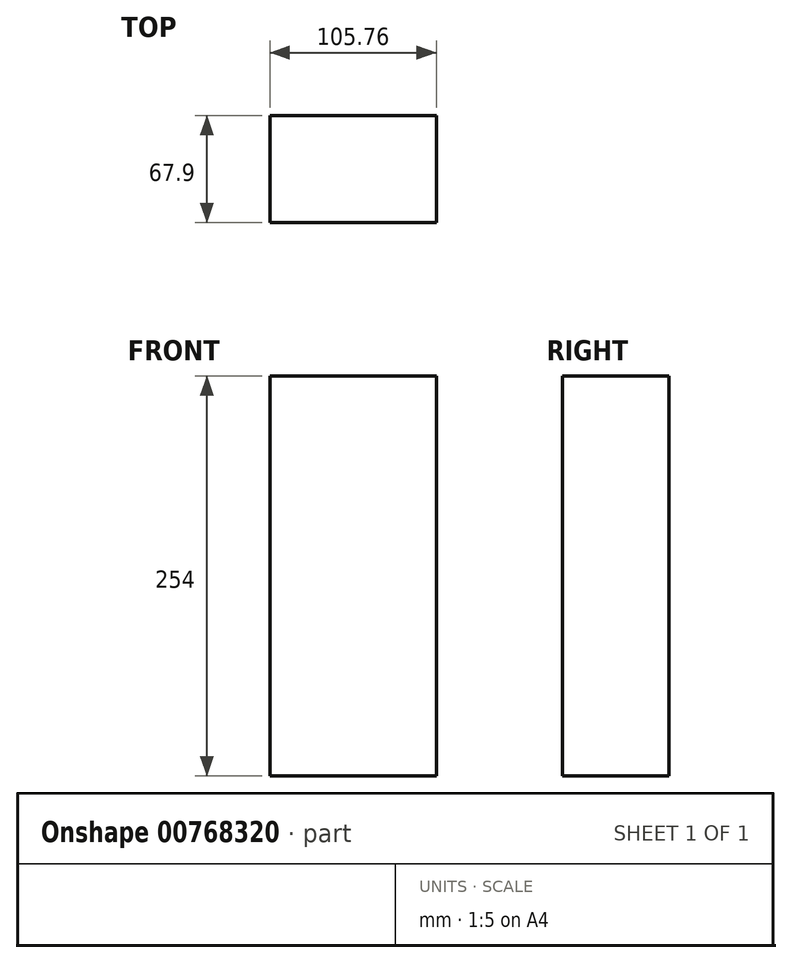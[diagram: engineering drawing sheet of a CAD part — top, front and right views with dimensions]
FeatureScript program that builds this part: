
annotation { "Feature Type Name" : "Feature", "Feature Type Description" : "" }
export const myFeature = defineFeature(function(context is Context, id is Id, definition is map)
    precondition{}
    {
        {
            var Q0;
            Q0=qCreatedBy(makeId("Top.planeOp"),FACE);
            var sketch = newSketch(context, id + "F0", { "sketchPlane" : qUnion([Q0])});
            skLineSegment(sketch, "E0.bottom", {"start": v(52.88, -33.95) * mm, "end": v(-52.88, -33.95) * mm});
            skLineSegment(sketch, "E0.top", {"start": v(52.88, 33.95) * mm, "end": v(-52.88, 33.95) * mm});
            skLineSegment(sketch, "E0.left", {"start": v(52.88, -33.95) * mm, "end": v(52.88, 33.95) * mm});
            skLineSegment(sketch, "E0.right", {"start": v(-52.88, -33.95) * mm, "end": v(-52.88, 33.95) * mm});
            skPoint(sketch, "E0.middle", {"position": v(0, 0) * mm});
            skSolve(sketch);
        }
        {
            var Q0;
            Q0 = qSketchRegion(id + "F0", true);
            extrude(context, id + "F1", {"entities" : qUnion([Q0]), "depth" : 254 * mm, "offsetDistance" : 25.4 * mm});
        }
    });
